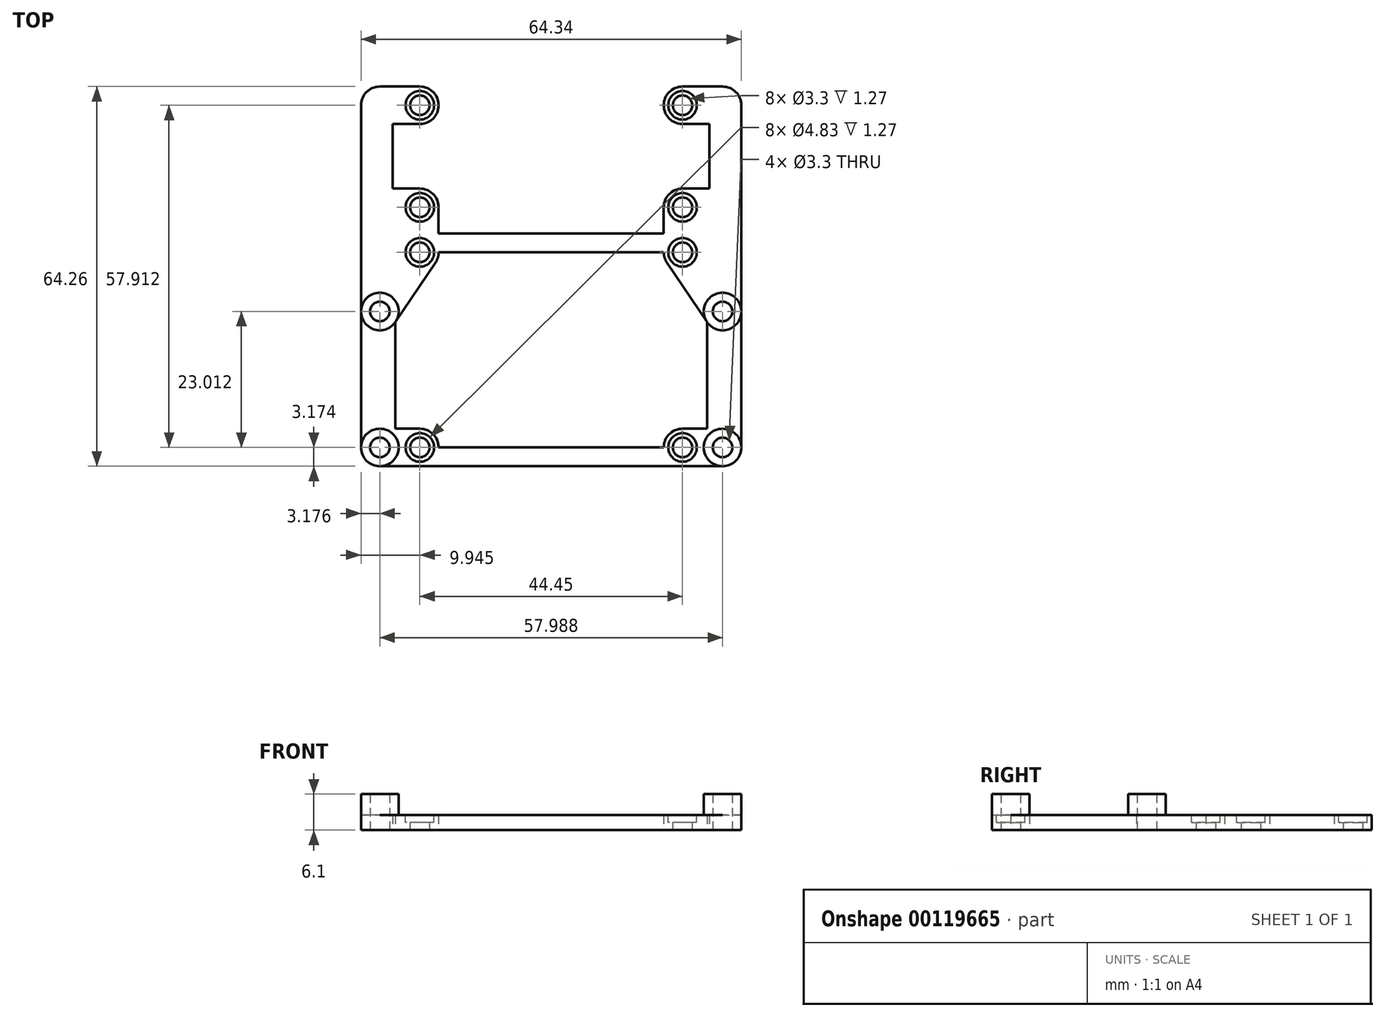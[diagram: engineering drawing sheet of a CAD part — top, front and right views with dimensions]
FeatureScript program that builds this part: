
annotation { "Feature Type Name" : "Feature", "Feature Type Description" : "" }
export const myFeature = defineFeature(function(context is Context, id is Id, definition is map)
    precondition{}
    {
        {
            var Q0;
            Q0=qCreatedBy(makeId("Top.planeOp"),FACE);
            var sketch = newSketch(context, id + "F0", { "sketchPlane" : qUnion([Q0])});
            skCircle(sketch, "E0", {"center": v(-29, 11.5) * mm, "radius": 3.18 * mm});
            skCircle(sketch, "E1", {"center": v(-29, -11.5) * mm, "radius": 3.18 * mm});
            skCircle(sketch, "E2", {"center": v(29, -11.5) * mm, "radius": 3.18 * mm});
            skCircle(sketch, "E3", {"center": v(29, 11.5) * mm, "radius": 3.18 * mm});
            skLineSegment(sketch, "E4", {"start": v(-29, -11.5) * mm, "end": v(-29, 11.5) * mm, "construction": true});
            skLineSegment(sketch, "E5", {"start": v(-29, -11.5) * mm, "end": v(29, -11.5) * mm, "construction": true});
            skPoint(sketch, "E6", {"position": v(-29, 0) * mm});
            skPoint(sketch, "E7", {"position": v(0, -11.5) * mm});
            skCircle(sketch, "E8", {"center": v(-22.22, -11.5) * mm, "radius": 3.18 * mm});
            skCircle(sketch, "E9", {"center": v(22.22, -11.5) * mm, "radius": 3.18 * mm});
            skCircle(sketch, "E10", {"center": v(22.23, 21.51) * mm, "radius": 3.18 * mm});
            skCircle(sketch, "E11", {"center": v(-22.23, 21.51) * mm, "radius": 3.18 * mm});
            skLineSegment(sketch, "E12", {"start": v(-22.22, -11.5) * mm, "end": v(22.22, -11.5) * mm, "construction": true});
            skCircle(sketch, "E13", {"center": v(22.23, 29.13) * mm, "radius": 3.18 * mm});
            skCircle(sketch, "E14", {"center": v(22.23, 46.4) * mm, "radius": 3.18 * mm});
            skCircle(sketch, "E15", {"center": v(-22.23, 46.4) * mm, "radius": 3.18 * mm});
            skCircle(sketch, "E16", {"center": v(-22.23, 29.13) * mm, "radius": 3.18 * mm});
            skSolve(sketch);
        }
        {
            var Q0;
            Q0=qCreatedBy(makeId("Top.planeOp"),FACE);
            var sketch = newSketch(context, id + "F1", { "sketchPlane" : qUnion([Q0])});
            skLineSegment(sketch, "E17", {"start": v(-29, -11.5) * mm, "end": v(-32.17, -11.5) * mm, "construction": true});
            skLineSegment(sketch, "E18", {"start": v(-29, -11.5) * mm, "end": v(-29, -14.68) * mm, "construction": true});
            skArc(sketch, "E19", {"start": v(-32.17, -11.5) * mm, "mid": v(-31.24, -13.75) * mm, "end": v(-29, -14.68) * mm});
            skLineSegment(sketch, "E20", {"start": v(-29, -14.68) * mm, "end": v(29, -14.68) * mm});
            skArc(sketch, "E21", {"start": v(29, -14.68) * mm, "mid": v(31.24, -13.75) * mm, "end": v(32.17, -11.5) * mm});
            skLineSegment(sketch, "E22", {"start": v(-19.6, 19.73) * mm, "end": v(-26.36, 9.73) * mm});
            skLineSegment(sketch, "E23", {"start": v(-26.36, 9.73) * mm, "end": v(-26.36, -8.33) * mm});
            skLineSegment(sketch, "E24", {"start": v(26.36, -8.33) * mm, "end": v(26.36, 9.73) * mm});
            skLineSegment(sketch, "E25", {"start": v(26.36, 9.73) * mm, "end": v(19.6, 19.73) * mm});
            skLineSegment(sketch, "E26", {"start": v(-26.36, -8.33) * mm, "end": v(-22.22, -8.33) * mm});
            skLineSegment(sketch, "E27", {"start": v(26.36, -8.33) * mm, "end": v(22.23, -8.33) * mm});
            skLineSegment(sketch, "E28", {"start": v(-19.05, 21.51) * mm, "end": v(19.05, 21.51) * mm});
            skArc(sketch, "E29", {"start": v(-19.6, 19.73) * mm, "mid": v(-19.19, 20.58) * mm, "end": v(-19.05, 21.51) * mm});
            skLineSegment(sketch, "E30", {"start": v(-19.05, -11.5) * mm, "end": v(19.05, -11.5) * mm});
            skArc(sketch, "E31", {"start": v(-19.05, -11.5) * mm, "mid": v(-19.98, -9.26) * mm, "end": v(-22.22, -8.33) * mm});
            skArc(sketch, "E32", {"start": v(22.23, -8.33) * mm, "mid": v(19.98, -9.26) * mm, "end": v(19.05, -11.5) * mm});
            skArc(sketch, "E33", {"start": v(19.05, 21.51) * mm, "mid": v(19.19, 20.58) * mm, "end": v(19.6, 19.73) * mm});
            skLineSegment(sketch, "E34", {"start": v(-32.17, -11.5) * mm, "end": v(-32.17, 46.4) * mm});
            skLineSegment(sketch, "E35", {"start": v(32.17, -11.5) * mm, "end": v(32.17, 46.4) * mm});
            skArc(sketch, "E36", {"start": v(-29, 49.58) * mm, "mid": v(-31.24, 48.65) * mm, "end": v(-32.17, 46.4) * mm});
            skArc(sketch, "E37", {"start": v(32.17, 46.4) * mm, "mid": v(31.24, 48.65) * mm, "end": v(29, 49.58) * mm});
            skLineSegment(sketch, "E38", {"start": v(-29, 49.58) * mm, "end": v(-22.22, 49.58) * mm});
            skLineSegment(sketch, "E39", {"start": v(29, 49.58) * mm, "end": v(22.23, 49.58) * mm});
            skLineSegment(sketch, "E40", {"start": v(-22.22, 32.3) * mm, "end": v(-26.8, 32.3) * mm});
            skLineSegment(sketch, "E41", {"start": v(-26.8, 32.3) * mm, "end": v(-26.8, 43.23) * mm});
            skLineSegment(sketch, "E42", {"start": v(-26.8, 43.23) * mm, "end": v(-22.22, 43.23) * mm});
            skArc(sketch, "E43", {"start": v(-22.22, 43.23) * mm, "mid": v(-19.05, 46.4) * mm, "end": v(-22.22, 49.58) * mm});
            skLineSegment(sketch, "E44", {"start": v(22.22, 43.23) * mm, "end": v(26.8, 43.23) * mm});
            skLineSegment(sketch, "E45", {"start": v(26.8, 43.23) * mm, "end": v(26.8, 32.3) * mm});
            skLineSegment(sketch, "E46", {"start": v(26.8, 32.3) * mm, "end": v(22.22, 32.3) * mm});
            skArc(sketch, "E47", {"start": v(22.22, 49.58) * mm, "mid": v(19.05, 46.4) * mm, "end": v(22.22, 43.23) * mm});
            skArc(sketch, "E48", {"start": v(-19.05, 29.13) * mm, "mid": v(-19.98, 31.38) * mm, "end": v(-22.22, 32.3) * mm});
            skArc(sketch, "E49", {"start": v(22.22, 32.3) * mm, "mid": v(19.98, 31.38) * mm, "end": v(19.05, 29.13) * mm});
            skLineSegment(sketch, "E50", {"start": v(19.05, 29.13) * mm, "end": v(19.05, 24.69) * mm});
            skLineSegment(sketch, "E51", {"start": v(19.05, 24.69) * mm, "end": v(-19.05, 24.69) * mm});
            skLineSegment(sketch, "E52", {"start": v(-19.05, 24.69) * mm, "end": v(-19.05, 29.13) * mm});
            skLineSegment(sketch, "E53", {"start": v(-19.05, 24.69) * mm, "end": v(-19.05, 21.51) * mm, "construction": true});
            skSolve(sketch);
        }
        {
            var Q0;
            Q0 = qSketchRegion(id + "F1", true);
            extrude(context, id + "F2", {"entities" : qUnion([Q0]), "depth" : 2.54 * mm});
        }
        {
            var Q0;
            Q0=makeQuery(id+"F2.opExtrude","CAP_FACE",FACE,{"disambiguationData":[OSD([sQuery(id+"F1.wireOp",EDGE,"UT721dgA-LXgf-lM4x-sxIu-eiIu3oGTLNxP"),sQuery(id+"F1.wireOp",EDGE,"L3nD7wWH-IeaR-HvAK-MyYc-0Ey1GP9vKFVT"),sQuery(id+"F1.wireOp",EDGE,"iHF76JLh-SPPY-mmE6-o1Ot-WfnKdtYiP4Ug"),sQuery(id+"F1.wireOp",EDGE,"l8rNpeWs-sFER-dhTt-w4BJ-CB6u86GkXCt5"),sQuery(id+"F1.wireOp",EDGE,"th4xKYtX-cNIn-TpR9-jSjG-bqeeJVTIbP3D"),sQuery(id+"F1.wireOp",EDGE,"E19"),sQuery(id+"F1.wireOp",EDGE,"E20"),sQuery(id+"F1.wireOp",EDGE,"E21"),sQuery(id+"F1.wireOp",EDGE,"kk6woftO-7xLb-CyRU-URZO-EuwESnr44vsJ"),sQuery(id+"F1.wireOp",EDGE,"ON7a2cab-CdFE-5vnm-QZcp-n5zNN012skjF"),sQuery(id+"F1.wireOp",EDGE,"57pyMCmq-X22D-mPmy-tZgG-RE2liGHA2OTy"),sQuery(id+"F1.wireOp",EDGE,"xfsUSbtM-dBAc-NcNb-o1Pn-OtX2ab3yEshs"),sQuery(id+"F1.wireOp",EDGE,"E22"),sQuery(id+"F1.wireOp",EDGE,"E23"),sQuery(id+"F1.wireOp",EDGE,"E24"),sQuery(id+"F1.wireOp",EDGE,"E25"),sQuery(id+"F1.wireOp",EDGE,"E26"),sQuery(id+"F1.wireOp",EDGE,"E27"),sQuery(id+"F1.wireOp",EDGE,"E28"),sQuery(id+"F1.wireOp",EDGE,"E29"),sQuery(id+"F1.wireOp",EDGE,"JYDqs9EX-hAmZ-nZsO-r3t3-9AUGzIAxMoHr"),sQuery(id+"F1.wireOp",EDGE,"E30"),sQuery(id+"F1.wireOp",EDGE,"E31"),sQuery(id+"F1.wireOp",EDGE,"E32")])],"isStart":false});
            var sketch = newSketch(context, id + "F3", { "sketchPlane" : qUnion([Q0])});
            skCircle(sketch, "E54", {"center": v(-29, -11.5) * mm, "radius": 3.17 * mm});
            skCircle(sketch, "E55", {"center": v(-29, 11.5) * mm, "radius": 3.17 * mm});
            skCircle(sketch, "E56", {"center": v(29, 11.5) * mm, "radius": 3.17 * mm});
            skCircle(sketch, "E57", {"center": v(29, -11.5) * mm, "radius": 3.17 * mm});
            skSolve(sketch);
        }
        {
            var Q0;
            Q0 = qSketchRegion(id + "F3", true);
            extrude(context, id + "F4", {"entities" : qUnion([Q0]), "operationType" : NewBodyOperationType.ADD, "depth" : 3.56 * mm});
        }
        {
            var Q0;
            Q0=makeQuery(id+"F2.opExtrude","CAP_FACE",FACE,{"disambiguationData":[OSD([sQuery(id+"F1.wireOp",EDGE,"UT721dgA-LXgf-lM4x-sxIu-eiIu3oGTLNxP"),sQuery(id+"F1.wireOp",EDGE,"L3nD7wWH-IeaR-HvAK-MyYc-0Ey1GP9vKFVT"),sQuery(id+"F1.wireOp",EDGE,"iHF76JLh-SPPY-mmE6-o1Ot-WfnKdtYiP4Ug"),sQuery(id+"F1.wireOp",EDGE,"l8rNpeWs-sFER-dhTt-w4BJ-CB6u86GkXCt5"),sQuery(id+"F1.wireOp",EDGE,"th4xKYtX-cNIn-TpR9-jSjG-bqeeJVTIbP3D"),sQuery(id+"F1.wireOp",EDGE,"E19"),sQuery(id+"F1.wireOp",EDGE,"E20"),sQuery(id+"F1.wireOp",EDGE,"E21"),sQuery(id+"F1.wireOp",EDGE,"kk6woftO-7xLb-CyRU-URZO-EuwESnr44vsJ"),sQuery(id+"F1.wireOp",EDGE,"ON7a2cab-CdFE-5vnm-QZcp-n5zNN012skjF"),sQuery(id+"F1.wireOp",EDGE,"57pyMCmq-X22D-mPmy-tZgG-RE2liGHA2OTy"),sQuery(id+"F1.wireOp",EDGE,"xfsUSbtM-dBAc-NcNb-o1Pn-OtX2ab3yEshs"),sQuery(id+"F1.wireOp",EDGE,"E22"),sQuery(id+"F1.wireOp",EDGE,"E23"),sQuery(id+"F1.wireOp",EDGE,"E24"),sQuery(id+"F1.wireOp",EDGE,"E25"),sQuery(id+"F1.wireOp",EDGE,"E26"),sQuery(id+"F1.wireOp",EDGE,"E27"),sQuery(id+"F1.wireOp",EDGE,"E28"),sQuery(id+"F1.wireOp",EDGE,"E29"),sQuery(id+"F1.wireOp",EDGE,"JYDqs9EX-hAmZ-nZsO-r3t3-9AUGzIAxMoHr"),sQuery(id+"F1.wireOp",EDGE,"E30"),sQuery(id+"F1.wireOp",EDGE,"E31"),sQuery(id+"F1.wireOp",EDGE,"E32")])],"isStart":true});
            var sketch = newSketch(context, id + "F5", { "sketchPlane" : qUnion([Q0])});
            skCircle(sketch, "E58", {"center": v(29, -11.5) * mm, "radius": 1.65 * mm});
            skCircle(sketch, "E59", {"center": v(22.23, -21.51) * mm, "radius": 1.65 * mm});
            skCircle(sketch, "E60", {"center": v(-22.23, -21.51) * mm, "radius": 1.65 * mm});
            skCircle(sketch, "E61", {"center": v(-29, -11.5) * mm, "radius": 1.65 * mm});
            skCircle(sketch, "E62", {"center": v(-29, 11.5) * mm, "radius": 1.65 * mm});
            skCircle(sketch, "E63", {"center": v(-22.22, 11.5) * mm, "radius": 1.65 * mm});
            skCircle(sketch, "E64", {"center": v(22.22, 11.5) * mm, "radius": 1.65 * mm});
            skCircle(sketch, "E65", {"center": v(29, 11.5) * mm, "radius": 1.65 * mm});
            skCircle(sketch, "E66", {"center": v(22.22, -29.13) * mm, "radius": 1.65 * mm});
            skCircle(sketch, "E67", {"center": v(22.22, -46.4) * mm, "radius": 1.65 * mm});
            skCircle(sketch, "E68", {"center": v(-22.22, -29.13) * mm, "radius": 1.65 * mm});
            skCircle(sketch, "E69", {"center": v(-22.22, -46.4) * mm, "radius": 1.65 * mm});
            skSolve(sketch);
        }
        {
            var Q0;
            Q0 = qSketchRegion(id + "F5", true);
            var Q1;
            Q1=makeQuery(id+"F4.opExtrude","CAP_FACE",FACE,{"disambiguationData":[OSD([sQuery(id+"F3.wireOp",EDGE,"E54")])],"isStart":false});
            extrude(context, id + "F6", {"entities" : qUnion([Q0]), "operationType" : NewBodyOperationType.REMOVE, "endBound" : BoundingType.UP_TO_SURFACE, "oppositeDirection" : true, "endBoundEntityFace" : qUnion([Q1]), "depth" : 25.4 * mm});
        }
        {
            var Q0;
            {var subQ0=sQuery(id+"F1.wireOp",EDGE,"E27");var subQ1=sQuery(id+"F1.wireOp",EDGE,"E24");var subQ2=sQuery(id+"F1.wireOp",EDGE,"E25");var subQ3=sQuery(id+"F1.wireOp",EDGE,"E23");var subQ4=sQuery(id+"F1.wireOp",EDGE,"E22");var subQ5=sQuery(id+"F1.wireOp",EDGE,"E31");var subQ6=sQuery(id+"F1.wireOp",EDGE,"E19");var subQ7=sQuery(id+"F1.wireOp",EDGE,"E35");var subQ8=sQuery(id+"F1.wireOp",EDGE,"E34");var subQ9=sQuery(id+"F1.wireOp",EDGE,"E32");var subQ10=sQuery(id+"F1.wireOp",EDGE,"E30");var subQ11=sQuery(id+"F1.wireOp",EDGE,"E26");var subQ12=sQuery(id+"F1.wireOp",EDGE,"E21");var subQ13=sQuery(id+"F1.wireOp",EDGE,"E20");var subQ14=makeQuery(id+"F2.opExtrude","CAP_FACE",FACE,{"disambiguationData":[OSD([subQ6,subQ13,subQ12,subQ4,subQ3,subQ1,subQ2,subQ11,subQ0,sQuery(id+"F1.wireOp",EDGE,"E28"),sQuery(id+"F1.wireOp",EDGE,"E29"),subQ10,subQ5,subQ9,sQuery(id+"F1.wireOp",EDGE,"E33"),subQ8,subQ7,sQuery(id+"F1.wireOp",EDGE,"E36"),sQuery(id+"F1.wireOp",EDGE,"E37"),sQuery(id+"F1.wireOp",EDGE,"E38"),sQuery(id+"F1.wireOp",EDGE,"E39"),sQuery(id+"F1.wireOp",EDGE,"E40"),sQuery(id+"F1.wireOp",EDGE,"E41"),sQuery(id+"F1.wireOp",EDGE,"E42"),sQuery(id+"F1.wireOp",EDGE,"E43"),sQuery(id+"F1.wireOp",EDGE,"E44"),sQuery(id+"F1.wireOp",EDGE,"E45"),sQuery(id+"F1.wireOp",EDGE,"E46"),sQuery(id+"F1.wireOp",EDGE,"E47"),sQuery(id+"F1.wireOp",EDGE,"9ZhXgbG9-1TM9-dVAF-EtKX-SdD3zufB1NPd"),sQuery(id+"F1.wireOp",EDGE,"E48"),sQuery(id+"F1.wireOp",EDGE,"E49")])],"isStart":false});Q0=makeQuery(id+"F4.boolean.opBoolean","SPLIT",FACE,{"disambiguationData":[TD([makeQuery(id+"F2.opExtrude","SWEPT_FACE",FACE,{"disambiguationData":[OSD([subQ6])]})])],"derivedFrom":subQ14});}
            var sketch = newSketch(context, id + "F7", { "sketchPlane" : qUnion([Q0])});
            skCircle(sketch, "E70", {"center": v(22.22, -11.5) * mm, "radius": 2.41 * mm});
            skCircle(sketch, "E71", {"center": v(22.23, 21.51) * mm, "radius": 2.41 * mm});
            skCircle(sketch, "E72", {"center": v(22.22, 29.13) * mm, "radius": 2.41 * mm});
            skCircle(sketch, "E73", {"center": v(22.22, 46.4) * mm, "radius": 2.41 * mm});
            skCircle(sketch, "E74", {"center": v(-22.22, 46.4) * mm, "radius": 2.41 * mm});
            skCircle(sketch, "E75", {"center": v(-22.22, 29.13) * mm, "radius": 2.41 * mm});
            skCircle(sketch, "E76", {"center": v(-22.23, 21.51) * mm, "radius": 2.41 * mm});
            skCircle(sketch, "E77", {"center": v(-22.22, -11.5) * mm, "radius": 2.41 * mm});
            skSolve(sketch);
        }
        {
            var Q0;
            Q0 = qSketchRegion(id + "F7", true);
            extrude(context, id + "F8", {"entities" : qUnion([Q0]), "operationType" : NewBodyOperationType.REMOVE, "oppositeDirection" : true, "depth" : 1.27 * mm});
        }
    });
